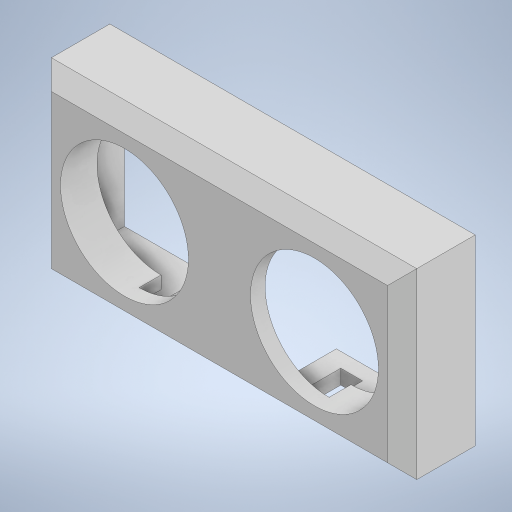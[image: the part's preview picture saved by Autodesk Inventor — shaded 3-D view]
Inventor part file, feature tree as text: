
AUTODESK INVENTOR PART (.ipt)
format: ipt  version: 2024.2 (Build 282272000, 272)  size: 298,496 bytes
history: native  units: mm
features: extrude x4, sketch x4, chamfer x1
ambient origin geometry x8: Origin, YZ Plane, XZ Plane, XY Plane, X Axis, Y Axis, Z Axis, Center Point
bodies: Solid1 (feature_tree)
feature tree (9):
  extrude  "Extrusion1"  Depth=17.5mm
  extrude  "Extrusion2"  Depth=50.0mm
  extrude  "Extrusion3"  Depth=12.0mm
  chamfer  "Chamfer2"  Distance=2.0mm
  extrude  "Extrusion4"  Depth=2.0mm
  sketch  "Sketch1"  dims[d0=17.5mm d1=17.5mm]
  sketch  "Sketch2"  dims[d2=26.0mm d3=50.0mm]
  sketch  "Sketch3"  dims[d4=25.0mm d5=12.0mm]
  sketch  "Sketch5"  dims[d6=12.5mm d7=2.0mm d8=0.0mm d12=2.0mm d14=46.0mm d15=2.0mm d16=21.0mm d17=8.0mm d18=0.0mm d19=12.0mm d20=19.0mm d21=2.0mm d22=2.0mm d23=25.0mm d24=3.0mm d25=0.0mm d26=2.0mm d27=2.0mm d28=45.0deg d29=3.0mm d31=3.0mm d33=17.2mm d34=13.4mm d35=1.5mm d36=3.0mm d37=0.0mm d38=2.0mm d39=1.5mm]
